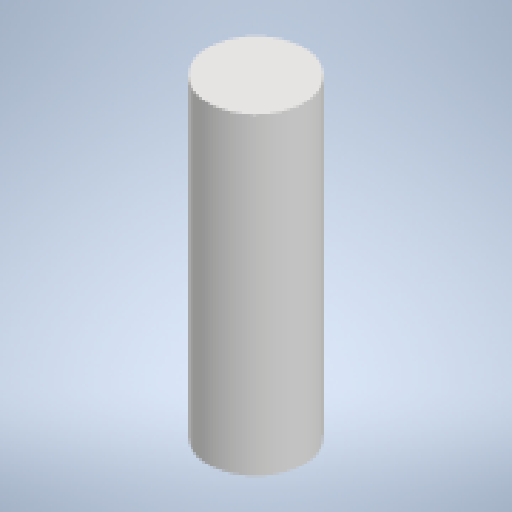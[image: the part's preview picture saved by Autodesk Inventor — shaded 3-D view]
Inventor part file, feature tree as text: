
AUTODESK INVENTOR PART (.ipt)
format: ipt  version: 2025.3 (Build 293356030, 356C)  size: 123,904 bytes
history: native  units: mm
features: extrude x1, sketch x1
ambient origin geometry x8: Origin, YZ Plane, XZ Plane, XY Plane, X Axis, Y Axis, Z Axis, Center Point
bodies: Solid1 (feature_tree)
feature tree (2):
  extrude  "Extrusion1"  Depth=7.5mm TaperAngle=0.0deg
  sketch  "Sketch1"  dims[d0=2.3mm d1=7.5mm d2=0.0mm]
